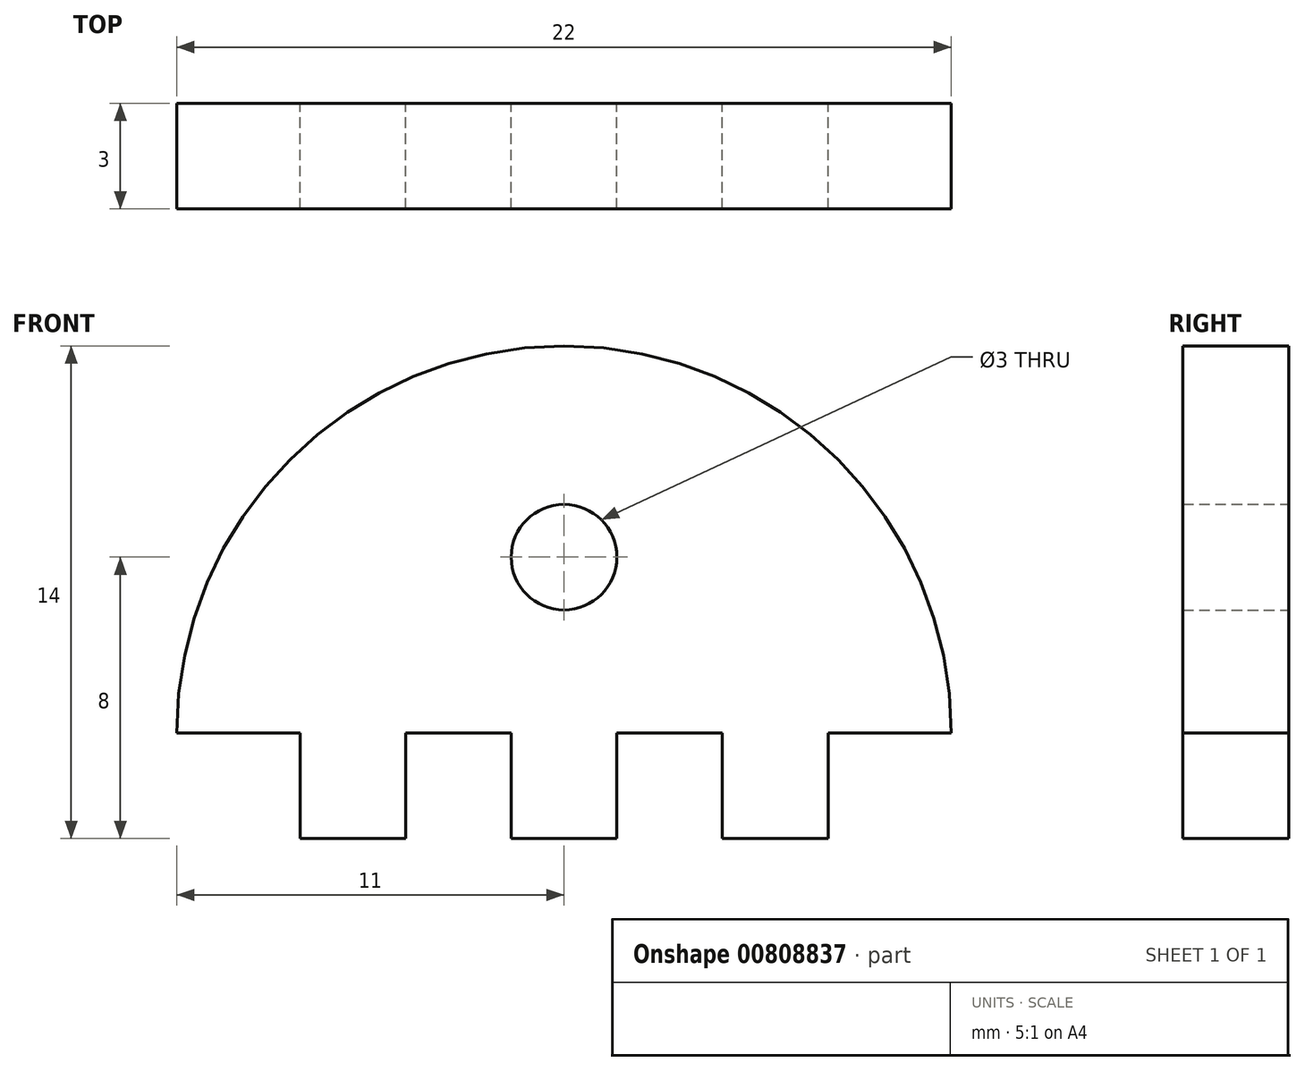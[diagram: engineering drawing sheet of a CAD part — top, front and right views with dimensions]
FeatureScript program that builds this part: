
annotation { "Feature Type Name" : "Feature", "Feature Type Description" : "" }
export const myFeature = defineFeature(function(context is Context, id is Id, definition is map)
    precondition{}
    {
        {
            var Q0;
            Q0=qCreatedBy(makeId("Front.planeOp"),FACE);
            var sketch = newSketch(context, id + "F0", { "sketchPlane" : qUnion([Q0])});
            skCircle(sketch, "E0", {"center": v(0, 0) * mm, "radius": 11 * mm});
            skLineSegment(sketch, "E1", {"start": v(-11, 0) * mm, "end": v(-6, 0) * mm});
            skLineSegment(sketch, "E2.bottom", {"start": v(-1.5, -3) * mm, "end": v(1.5, -3) * mm});
            skLineSegment(sketch, "E2.left", {"start": v(-1.5, -3) * mm, "end": v(-1.5, 0) * mm});
            skLineSegment(sketch, "E2.right", {"start": v(1.5, -3) * mm, "end": v(1.5, 0) * mm});
            skLineSegment(sketch, "E3.bottom", {"start": v(-4.5, -3) * mm, "end": v(-7.5, -3) * mm});
            skLineSegment(sketch, "E3.top", {"start": v(-4.5, 3) * mm, "end": v(-7.5, 3) * mm});
            skLineSegment(sketch, "E3.left", {"start": v(-4.5, -3) * mm, "end": v(-4.5, 0) * mm});
            skLineSegment(sketch, "E3.right", {"start": v(-7.5, -3) * mm, "end": v(-7.5, 3) * mm});
            skPoint(sketch, "E3.middle", {"position": v(-6, 0) * mm});
            skLineSegment(sketch, "E4.bottom", {"start": v(4.5, -3) * mm, "end": v(7.5, -3) * mm});
            skLineSegment(sketch, "E4.top", {"start": v(4.5, 3) * mm, "end": v(7.5, 3) * mm});
            skLineSegment(sketch, "E4.left", {"start": v(4.5, -3) * mm, "end": v(4.5, 0) * mm});
            skLineSegment(sketch, "E4.right", {"start": v(7.5, -3) * mm, "end": v(7.5, 3) * mm});
            skPoint(sketch, "E4.middle", {"position": v(6, 0) * mm});
            skCircle(sketch, "E5", {"center": v(0, 5) * mm, "radius": 1.5 * mm});
            skPoint(sketch, "E6.orphan", {"position": v(-1.5, 3) * mm});
            skPoint(sketch, "E7.orphan", {"position": v(1.5, 3) * mm});
            skLineSegment(sketch, "E8.trimOffspring", {"start": v(1.5, 0) * mm, "end": v(4.5, 0) * mm});
            skLineSegment(sketch, "E9.trimOffspring", {"start": v(-4.5, 0) * mm, "end": v(-1.5, 0) * mm});
            skLineSegment(sketch, "E10.trimOffspring", {"start": v(6, 0) * mm, "end": v(11, 0) * mm});
            skSolve(sketch);
        }
        {
            var Q0;
            {var subQ5=sQuery(id+"F0.wireOp",EDGE,"E2.top");Q0=makeQuery(id+"F0.imprint","IMPRINT",FACE,{"disambiguationData":[TD([[makeQuery(id+"F0.imprint","IMPRINT",EDGE,{"derivedFrom":subQ5}),1.0]])]});}
            var Q1;
            {var subQ5=sQuery(id+"F0.wireOp",EDGE,"E3.bottom");Q1=makeQuery(id+"F0.imprint","IMPRINT",FACE,{"disambiguationData":[TD([[makeQuery(id+"F0.imprint","IMPRINT",EDGE,{"derivedFrom":subQ5}),-1.0]])]});}
            var Q2;
            {var subQ5=sQuery(id+"F0.wireOp",EDGE,"E2.bottom");Q2=makeQuery(id+"F0.imprint","IMPRINT",FACE,{"disambiguationData":[TD([[makeQuery(id+"F0.imprint","IMPRINT",EDGE,{"derivedFrom":subQ5}),1.0]])]});}
            var Q3;
            {var subQ5=sQuery(id+"F0.wireOp",EDGE,"E4.bottom");Q3=makeQuery(id+"F0.imprint","IMPRINT",FACE,{"disambiguationData":[TD([[makeQuery(id+"F0.imprint","IMPRINT",EDGE,{"derivedFrom":subQ5}),1.0]])]});}
            var Q4;
            {var subQ5=sQuery(id+"F0.wireOp",EDGE,"E4.top");Q4=makeQuery(id+"F0.imprint","IMPRINT",FACE,{"disambiguationData":[TD([[makeQuery(id+"F0.imprint","IMPRINT",EDGE,{"derivedFrom":subQ5}),-1.0]])]});}
            var Q5;
            {var subQ5=sQuery(id+"F0.wireOp",EDGE,"E2.top");Q5=makeQuery(id+"F0.imprint","IMPRINT",FACE,{"disambiguationData":[TD([[makeQuery(id+"F0.imprint","IMPRINT",EDGE,{"derivedFrom":subQ5}),-1.0]])]});}
            var Q6;
            {var subQ5=sQuery(id+"F0.wireOp",EDGE,"E3.top");Q6=makeQuery(id+"F0.imprint","IMPRINT",FACE,{"disambiguationData":[TD([[makeQuery(id+"F0.imprint","IMPRINT",EDGE,{"derivedFrom":subQ5}),1.0]])]});}
            extrude(context, id + "F1", {"entities" : qUnion([Q0, Q1, Q2, Q3, Q4, Q5, Q6]), "depth" : 3 * mm, "offsetDistance" : 25 * mm});
        }
    });
